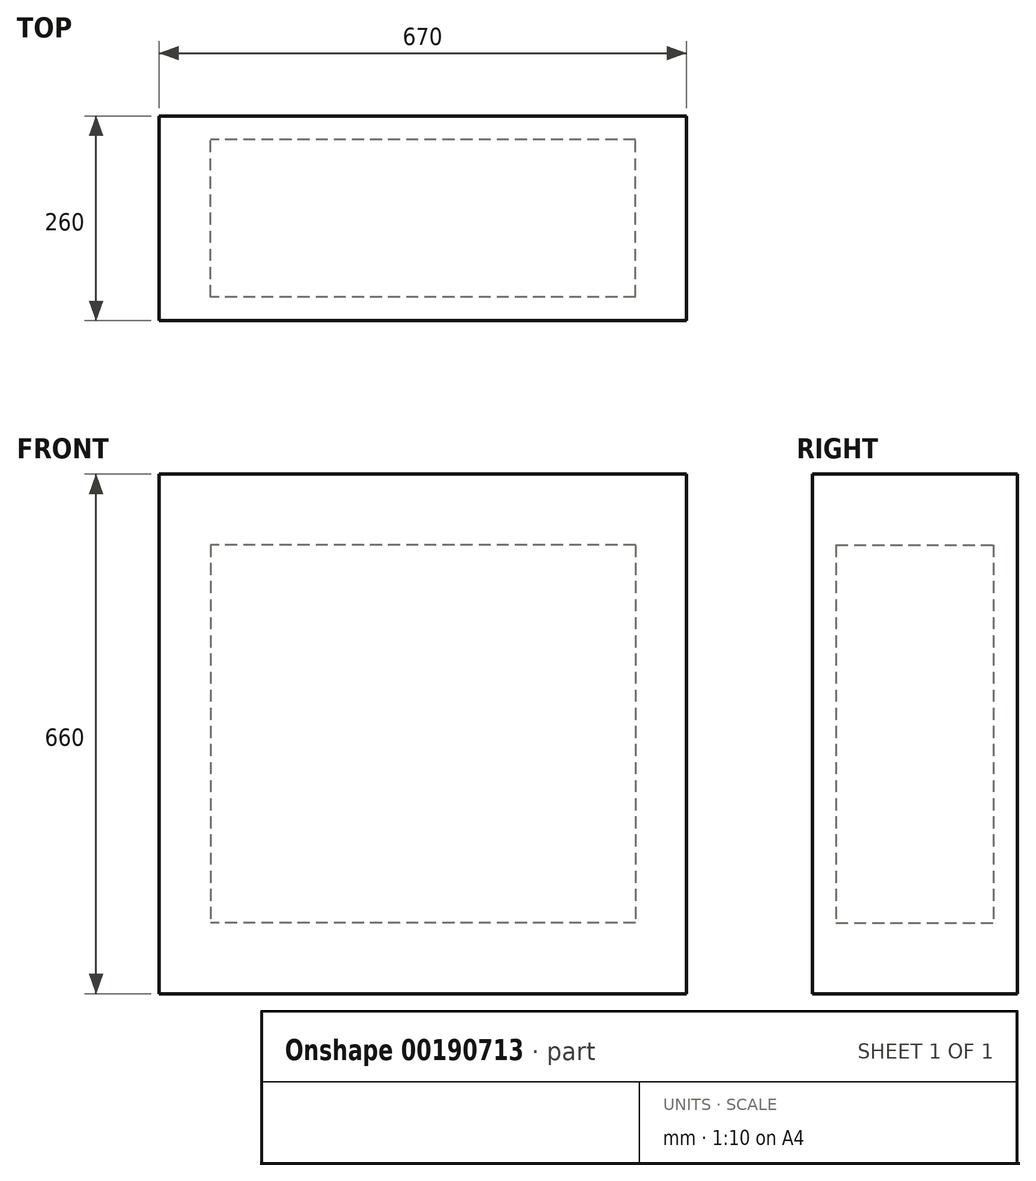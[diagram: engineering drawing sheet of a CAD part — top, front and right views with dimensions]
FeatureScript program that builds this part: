
annotation { "Feature Type Name" : "Feature", "Feature Type Description" : "" }
export const myFeature = defineFeature(function(context is Context, id is Id, definition is map)
    precondition{}
    {
        {
            var Q0;
            Q0=qCreatedBy(makeId("Top.planeOp"),FACE);
            cPlane(context, id + "F0", {"entities" : qUnion([Q0]), "cplaneType" : CPlaneType.OFFSET, "offset" : 90 * mm, "width" : 150 * mm, "height" : 150 * mm});
        }
        {
            var Q0;
            Q0=qCreatedBy(id+"F0.planeOp",FACE);
            var sketch = newSketch(context, id + "F1", { "sketchPlane" : qUnion([Q0])});
            skLineSegment(sketch, "E0.bottom", {"start": v(270, -100) * mm, "end": v(-270, -100) * mm});
            skLineSegment(sketch, "E0.top", {"start": v(270, 100) * mm, "end": v(-270, 100) * mm});
            skLineSegment(sketch, "E0.left", {"start": v(270, -100) * mm, "end": v(270, 100) * mm});
            skLineSegment(sketch, "E0.right", {"start": v(-270, -100) * mm, "end": v(-270, 100) * mm});
            skPoint(sketch, "E0.middle", {"position": v(0, 0) * mm});
            skSolve(sketch);
        }
        {
            var Q0;
            Q0=makeQuery(id+"F1.imprint","IMPRINT",FACE,{"disambiguationData":[TD([[makeQuery(id+"F1.imprint","IMPRINT",EDGE,{"derivedFrom":sQuery(id+"F1.wireOp",EDGE,"E0.bottom")}),-1.0]])]});
            extrude(context, id + "F2", {"entities" : qUnion([Q0]), "depth" : 480 * mm});
        }
        {
            var Q0;
            Q0=qCreatedBy(makeId("Top.planeOp"),FACE);
            var sketch = newSketch(context, id + "F3", { "sketchPlane" : qUnion([Q0])});
            skLineSegment(sketch, "E1.bottom", {"start": v(-335, -130) * mm, "end": v(335, -130) * mm});
            skLineSegment(sketch, "E1.top", {"start": v(-335, 130) * mm, "end": v(335, 130) * mm});
            skLineSegment(sketch, "E1.left", {"start": v(-335, -130) * mm, "end": v(-335, 130) * mm});
            skLineSegment(sketch, "E1.right", {"start": v(335, -130) * mm, "end": v(335, 130) * mm});
            skPoint(sketch, "E1.middle", {"position": v(0, 0) * mm});
            skSolve(sketch);
        }
        {
            var Q0;
            Q0 = qSketchRegion(id + "F3", true);
            extrude(context, id + "F4", {"entities" : qUnion([Q0]), "depth" : 660 * mm});
        }
    });
